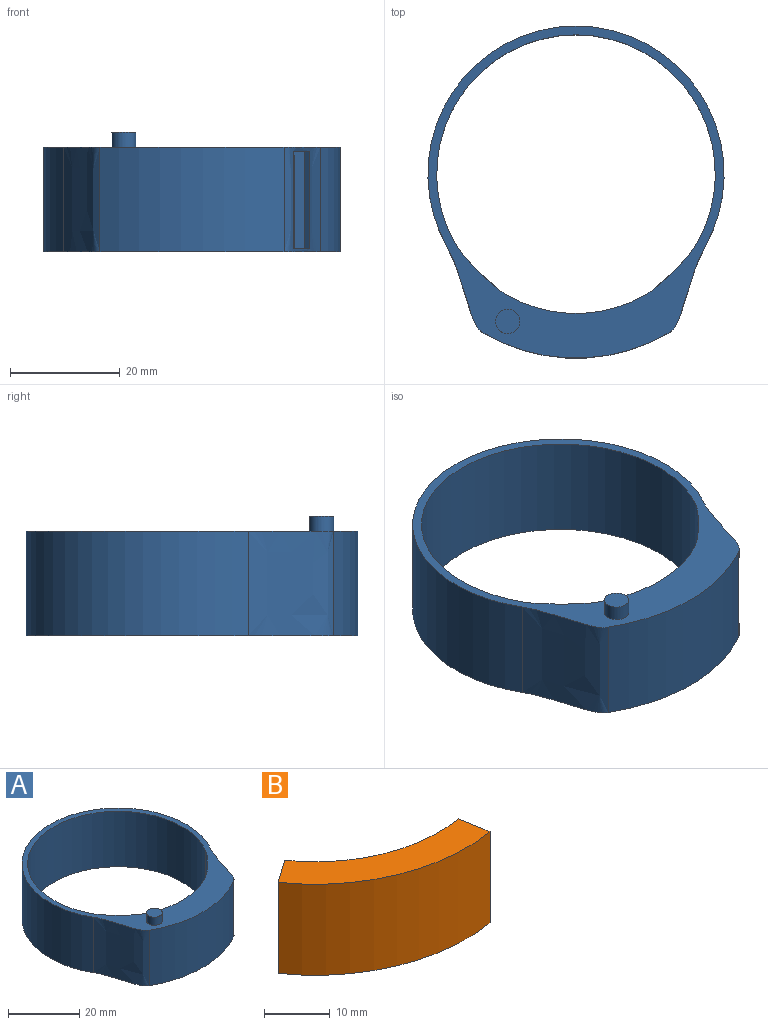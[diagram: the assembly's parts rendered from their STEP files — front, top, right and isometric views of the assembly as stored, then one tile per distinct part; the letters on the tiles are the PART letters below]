
ASSEMBLY  parts=2 mates=1
PART A: 18 faces, bbox 54x60.6x21.8 mm
  f0: plane 60.56x54.02mm, normal (0,0,1), area 542.2mm2, adj f1,f3,f4,f5,f6,f7,f8,f9
  f1: cylinder r=25.4mm len=50.8mm, axis (0,0,-1), area 2026.8mm2, adj f0,f2,f7,f8
  f2: plane 60.56x54.02mm, normal (0,0,-1), area 557.6mm2, adj f1,f3,f4,f5,f6,f7,f8,f9
  f3: cylinder r=27.01mm len=54.02mm, axis (0,0,-1), area 2155.2mm2, adj f0,f2,f6,f9
  f4: cylinder r=25.4mm len=25.4mm, axis (0,0,-1), area 506.7mm2, adj f0,f2,f7,f8
  f5: cylinder r=33.55mm len=33.55mm, axis (0,0,-1), area 669.3mm2, adj f0,f2,f6,f9
  f6: bspline ~19.05x15.55mm, area 326.1mm2, adj f0,f2,f3,f5
  f7: bspline ~19.05x9.3mm, area 252.2mm2, adj f0,f1,f2,f4
  f8: bspline ~19.05x9.3mm, area 252.2mm2, adj f0,f1,f2,f4
  f9: bspline ~19.05x15.55mm, area 160.8mm2, adj f0,f2,f3,f5,f11,f12,f13,f15
  f10: cylinder r=26.67mm len=31.7mm, axis (0,0,1), area 620.7mm2, adj f11,f13,f14,f15
  f11: plane 35.26x15.5mm, normal (0,0,-1), area 210.6mm2, adj f9,f10,f12,f14,f15
  f12: cylinder r=32.64mm len=32.37mm, axis (0,0,1), area 604.5mm2, adj f9,f11,f13,f14
  f13: plane 35.26x15.5mm, normal (0,0,1), area 210.6mm2, adj f9,f10,f12,f14,f15
  f14: plane 17.78x5.41mm, normal (0.91,-0.42,0), area 106.1mm2, adj f10,f11,f12,f13
  f15: plane 17.78x1.04mm, normal (-0.64,-0.77,0), area 24mm2, adj f9,f10,f11,f13
  f16: cylinder r=2.22mm len=4.44mm, axis (0,0,-1), area 39mm2, adj f0,f17
  f17: plane 4.44x4.44mm, normal (0,0,1), area 15.5mm2, adj f16
PART B: 6 faces, bbox 32.4x17.3x17 mm
  f0: cylinder r=26.67mm len=26.48mm, axis (0,0,-1), area 514.9mm2, adj f1,f3,f4,f5
  f1: plane 32.35x17.29mm, normal (0,0,1), area 198.9mm2, adj f0,f2,f4,f5
  f2: cylinder r=32.59mm len=32.35mm, axis (0,0,-1), area 629.2mm2, adj f1,f3,f4,f5
  f3: plane 32.35x17.29mm, normal (0,0,-1), area 198.9mm2, adj f0,f2,f4,f5
  f4: plane 17.02x5.83mm, normal (0.98,0.17,0), area 100.7mm2, adj f0,f1,f2,f3
  f5: plane 17.02x4.85mm, normal (-0.57,0.82,0), area 100.7mm2, adj f0,f1,f2,f3
PLACE A t=(-4.56,4.18,-4.21)mm fixed
PLACE B rot(axis=(0,0,1),25deg) t=(-4.56,4.18,-3.66)mm
MATE revolute A.f1 <-> B.f0  axis (0,0,1) through (-4.56,4.18,-3.66)mm
